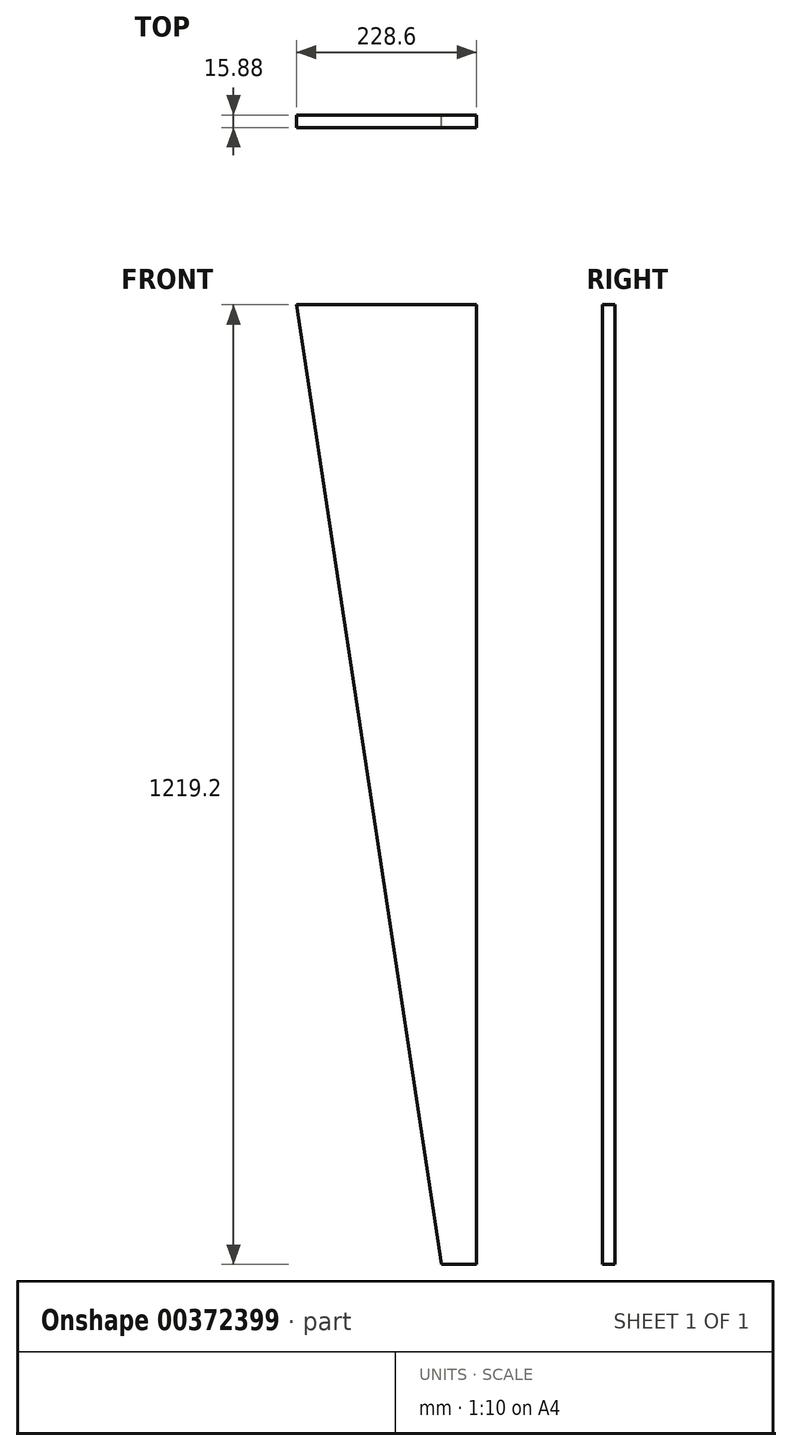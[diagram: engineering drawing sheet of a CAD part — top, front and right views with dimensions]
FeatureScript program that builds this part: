
annotation { "Feature Type Name" : "Feature", "Feature Type Description" : "" }
export const myFeature = defineFeature(function(context is Context, id is Id, definition is map)
    precondition{}
    {
        {
            var Q0;
            Q0=qCreatedBy(makeId("Front.planeOp"),FACE);
            var sketch = newSketch(context, id + "F0", { "sketchPlane" : qUnion([Q0])});
            skLineSegment(sketch, "E0.top", {"start": v(-942.97, 565.15) * mm, "end": v(-1171.58, 565.15) * mm});
            skPoint(sketch, "E0.middle", {"position": v(0, 0) * mm});
            skPoint(sketch, "E1.orphan", {"position": v(-1127.12, -565.15) * mm});
            skLineSegment(sketch, "E2", {"start": v(-942.97, -654.05) * mm, "end": v(-942.97, 565.15) * mm});
            skPoint(sketch, "E0.left.end.orphan", {"position": v(1127.13, 565.15) * mm});
            skPoint(sketch, "E0.left.start.orphan", {"position": v(1171.57, -565.15) * mm});
            skLineSegment(sketch, "E3", {"start": v(-942.97, -654.05) * mm, "end": v(-987.42, -654.05) * mm});
            skLineSegment(sketch, "E4", {"start": v(-987.42, -654.05) * mm, "end": v(-1171.58, 565.15) * mm});
            skSolve(sketch);
        }
        {
            var Q0;
            Q0=qSketchRegion(id+"F0",true);
            extrude(context, id + "F1", {"entities" : qUnion([Q0]), "depth" : 15.88 * mm});
        }
    });
